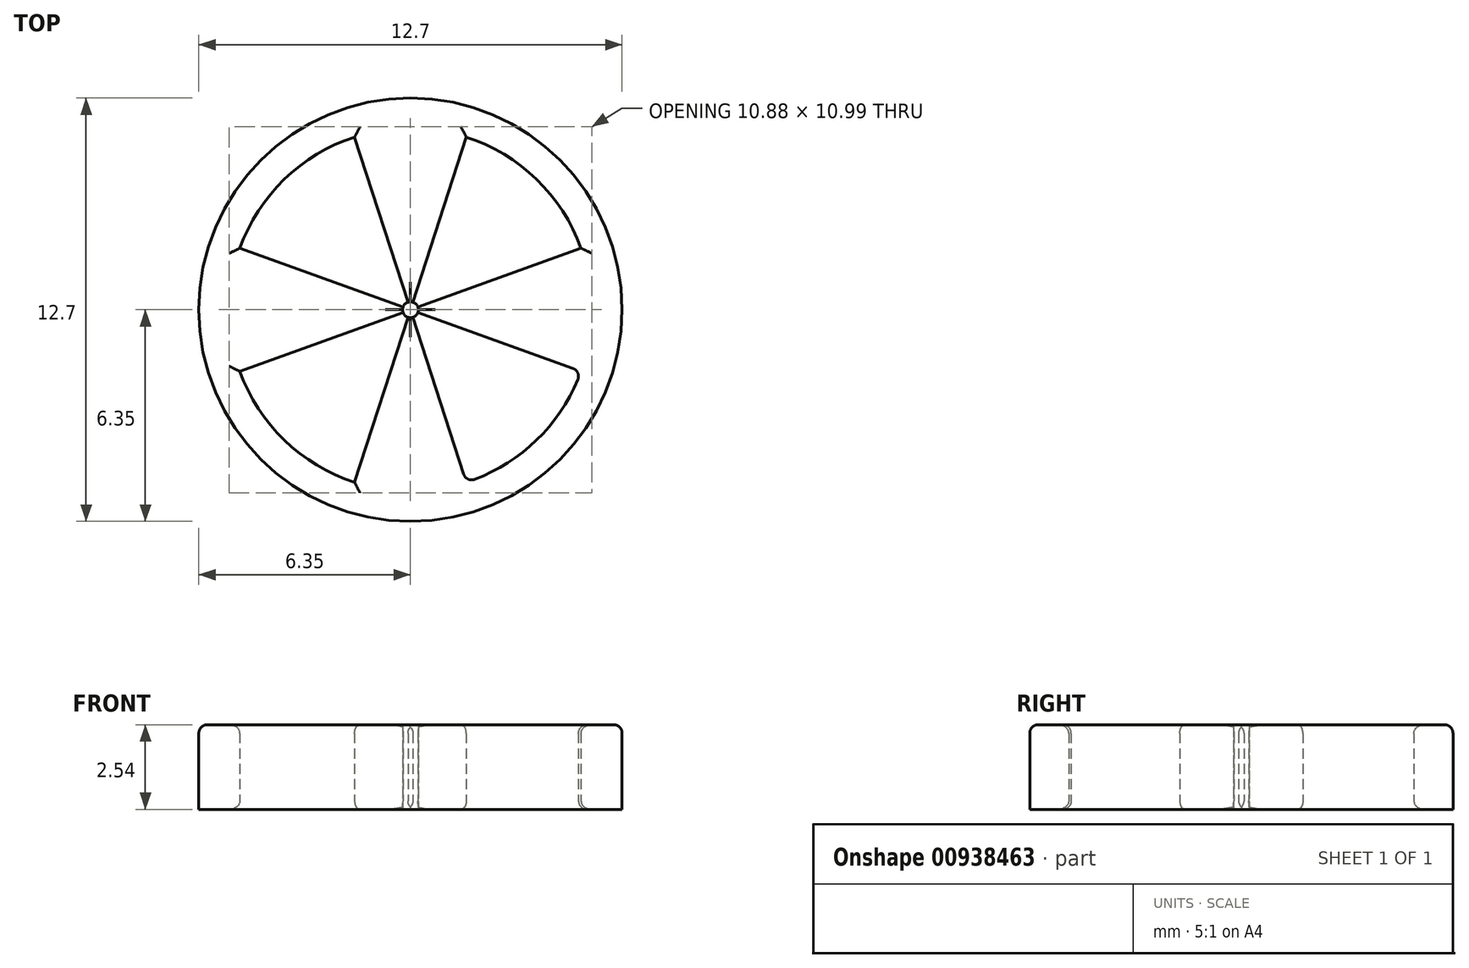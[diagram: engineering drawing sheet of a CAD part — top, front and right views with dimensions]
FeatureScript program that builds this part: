
annotation { "Feature Type Name" : "Feature", "Feature Type Description" : "" }
export const myFeature = defineFeature(function(context is Context, id is Id, definition is map)
    precondition{}
    {
        {
            var Q0;
            Q0=qCreatedBy(makeId("Top.planeOp"),FACE);
            var sketch = newSketch(context, id + "F0", { "sketchPlane" : qUnion([Q0])});
            skCircle(sketch, "E0", {"center": v(0, 0) * mm, "radius": 5.44 * mm});
            skLineSegment(sketch, "E1", {"start": v(0, 0) * mm, "end": v(-5.44, 0) * mm});
            skLineSegment(sketch, "E2", {"start": v(-5.44, 0) * mm, "end": v(5.44, 0) * mm});
            skLineSegment(sketch, "E3", {"start": v(0, 5.44) * mm, "end": v(0, -5.44) * mm});
            skLineSegment(sketch, "E4", {"start": v(0, 0) * mm, "end": v(-5.12, 1.85) * mm});
            skLineSegment(sketch, "E5.MirrorCS", {"start": v(0, 0) * mm, "end": v(5.12, 1.85) * mm});
            skLineSegment(sketch, "E6.MirrorCS", {"start": v(0, 0) * mm, "end": v(-5.12, -1.85) * mm});
            skLineSegment(sketch, "E7.MirrorCS", {"start": v(0, 0) * mm, "end": v(5.12, -1.85) * mm});
            skLineSegment(sketch, "E8", {"start": v(0, 0) * mm, "end": v(1.68, -5.18) * mm});
            skLineSegment(sketch, "E9.MirrorCS", {"start": v(0, 0) * mm, "end": v(-1.68, -5.18) * mm});
            skCircle(sketch, "E10.0", {"center": v(0, 0) * mm, "radius": 6.35 * mm});
            skCircle(sketch, "E11", {"center": v(0, 0) * mm, "radius": 0.24 * mm});
            skLineSegment(sketch, "E12.MirrorCS", {"start": v(0, 0) * mm, "end": v(1.68, 5.18) * mm});
            skLineSegment(sketch, "E13.MirrorCS", {"start": v(0, 0) * mm, "end": v(-1.68, 5.18) * mm});
            skSolve(sketch);
        }
        {
            var Q0;
            Q0=makeQuery(id+"F0.imprint","IMPRINT",FACE,{"disambiguationData":[TD([[makeQuery(id+"F0.imprint","IMPRINT",EDGE,{"derivedFrom":sQuery(id+"F0.wireOp",EDGE,"E10.0")}),1.0]])]});
            var Q1;
            {var subQ0=sQuery(id+"F0.wireOp",EDGE,"E3");var subQ1=sQuery(id+"F0.wireOp",EDGE,"E0");var subQ2=makeQuery(id+"F0.imprint","INTERSECT",VERTEX,{"disambiguationData":[OD(1.0)],"derivedFrom":[subQ1,subQ0]});Q1=makeQuery(id+"F0.imprint","IMPRINT",FACE,{"disambiguationData":[TD([[makeQuery(id+"F0.imprint","IMPRINT",EDGE,{"disambiguationData":[TD([[subQ2,-1.0]])],"derivedFrom":subQ1}),1.0]])]});}
            var Q2;
            {var subQ0=sQuery(id+"F0.wireOp",EDGE,"E9.MirrorCS");var subQ1=sQuery(id+"F0.wireOp",EDGE,"E0");var subQ2=makeQuery(id+"F0.imprint","INTERSECT",VERTEX,{"derivedFrom":[subQ1,subQ0]});Q2=makeQuery(id+"F0.imprint","IMPRINT",FACE,{"disambiguationData":[TD([[makeQuery(id+"F0.imprint","IMPRINT",EDGE,{"disambiguationData":[TD([[subQ2,-1.0]])],"derivedFrom":subQ1}),1.0]])]});}
            var Q3;
            {var subQ0=sQuery(id+"F0.wireOp",EDGE,"E4");var subQ1=sQuery(id+"F0.wireOp",EDGE,"E0");var subQ2=makeQuery(id+"F0.imprint","INTERSECT",VERTEX,{"derivedFrom":[subQ1,subQ0]});Q3=makeQuery(id+"F0.imprint","IMPRINT",FACE,{"disambiguationData":[TD([[makeQuery(id+"F0.imprint","IMPRINT",EDGE,{"disambiguationData":[TD([[subQ2,-1.0]])],"derivedFrom":subQ1}),1.0]])]});}
            var Q4;
            {var subQ0=sQuery(id+"F0.wireOp",EDGE,"E1");var subQ1=sQuery(id+"F0.wireOp",EDGE,"E0");var subQ2=makeQuery(id+"F0.imprint","INTERSECT",VERTEX,{"derivedFrom":[subQ1,subQ0]});Q4=makeQuery(id+"F0.imprint","IMPRINT",FACE,{"disambiguationData":[TD([[makeQuery(id+"F0.imprint","IMPRINT",EDGE,{"disambiguationData":[TD([[subQ2,-1.0]])],"derivedFrom":subQ1}),1.0]])]});}
            var Q5;
            {var subQ0=sQuery(id+"F0.wireOp",EDGE,"E5.MirrorCS");var subQ1=sQuery(id+"F0.wireOp",EDGE,"E0");var subQ2=makeQuery(id+"F0.imprint","INTERSECT",VERTEX,{"derivedFrom":[subQ1,subQ0]});Q5=makeQuery(id+"F0.imprint","IMPRINT",FACE,{"disambiguationData":[TD([[makeQuery(id+"F0.imprint","IMPRINT",EDGE,{"disambiguationData":[TD([[subQ2,1.0]])],"derivedFrom":subQ1}),1.0]])]});}
            var Q6;
            {var subQ0=sQuery(id+"F0.wireOp",EDGE,"E2");var subQ1=sQuery(id+"F0.wireOp",EDGE,"E0");var subQ2=makeQuery(id+"F0.imprint","INTERSECT",VERTEX,{"derivedFrom":[subQ1,subQ0]});Q6=makeQuery(id+"F0.imprint","IMPRINT",FACE,{"disambiguationData":[TD([[makeQuery(id+"F0.imprint","IMPRINT",EDGE,{"disambiguationData":[TD([[subQ2,1.0]])],"derivedFrom":subQ1}),1.0]])]});}
            var Q7;
            {var subQ0=sQuery(id+"F0.wireOp",EDGE,"E3");var subQ1=sQuery(id+"F0.wireOp",EDGE,"E0");var subQ2=makeQuery(id+"F0.imprint","INTERSECT",VERTEX,{"disambiguationData":[OD(0.0)],"derivedFrom":[subQ1,subQ0]});Q7=makeQuery(id+"F0.imprint","IMPRINT",FACE,{"disambiguationData":[TD([[makeQuery(id+"F0.imprint","IMPRINT",EDGE,{"disambiguationData":[TD([[subQ2,-1.0]])],"derivedFrom":subQ1}),1.0]])]});}
            var Q8;
            {var subQ0=sQuery(id+"F0.wireOp",EDGE,"E12.MirrorCS");var subQ1=sQuery(id+"F0.wireOp",EDGE,"E0");var subQ2=makeQuery(id+"F0.imprint","INTERSECT",VERTEX,{"derivedFrom":[subQ1,subQ0]});Q8=makeQuery(id+"F0.imprint","IMPRINT",FACE,{"disambiguationData":[TD([[makeQuery(id+"F0.imprint","IMPRINT",EDGE,{"disambiguationData":[TD([[subQ2,-1.0]])],"derivedFrom":subQ1}),1.0]])]});}
            extrude(context, id + "F1", {"entities" : qUnion([Q0, Q1, Q2, Q3, Q4, Q5, Q6, Q7, Q8]), "depth" : 2.54 * mm, "offsetDistance" : 25.4 * mm});
        }
        {
            var Q0;
            {var subQ0=sQuery(id+"F0.wireOp",EDGE,"E11");var subQ1=sQuery(id+"F0.wireOp",EDGE,"E1");var subQ2=makeQuery(id+"F0.imprint","INTERSECT",VERTEX,{"derivedFrom":[subQ1,subQ0]});Q0=makeQuery(id+"F0.imprint","IMPRINT",FACE,{"disambiguationData":[TD([[makeQuery(id+"F0.imprint","IMPRINT",EDGE,{"disambiguationData":[TD([[subQ2,-1.0]])],"derivedFrom":subQ0}),1.0]])]});}
            var Q1;
            {var subQ0=sQuery(id+"F0.wireOp",EDGE,"E11");var subQ1=sQuery(id+"F0.wireOp",EDGE,"E1");var subQ2=makeQuery(id+"F0.imprint","INTERSECT",VERTEX,{"derivedFrom":[subQ1,subQ0]});Q1=makeQuery(id+"F0.imprint","IMPRINT",FACE,{"disambiguationData":[TD([[makeQuery(id+"F0.imprint","IMPRINT",EDGE,{"disambiguationData":[TD([[subQ2,1.0]])],"derivedFrom":subQ0}),1.0]])]});}
            var Q2;
            {var subQ0=sQuery(id+"F0.wireOp",EDGE,"E11");var subQ1=sQuery(id+"F0.wireOp",EDGE,"E2");var subQ2=makeQuery(id+"F0.imprint","INTERSECT",VERTEX,{"derivedFrom":[subQ1,subQ0]});Q2=makeQuery(id+"F0.imprint","IMPRINT",FACE,{"disambiguationData":[TD([[makeQuery(id+"F0.imprint","IMPRINT",EDGE,{"disambiguationData":[TD([[subQ2,-1.0]])],"derivedFrom":subQ0}),1.0]])]});}
            var Q3;
            {var subQ0=sQuery(id+"F0.wireOp",EDGE,"E11");var subQ1=sQuery(id+"F0.wireOp",EDGE,"E2");var subQ2=makeQuery(id+"F0.imprint","INTERSECT",VERTEX,{"derivedFrom":[subQ1,subQ0]});Q3=makeQuery(id+"F0.imprint","IMPRINT",FACE,{"disambiguationData":[TD([[makeQuery(id+"F0.imprint","IMPRINT",EDGE,{"disambiguationData":[TD([[subQ2,1.0]])],"derivedFrom":subQ0}),1.0]])]});}
            var Q4;
            {var subQ0=sQuery(id+"F0.wireOp",EDGE,"E12.MirrorCS");var subQ3=sQuery(id+"F0.wireOp",EDGE,"E11");var subQ5=makeQuery(id+"F0.imprint","INTERSECT",VERTEX,{"derivedFrom":[subQ3,subQ0]});Q4=makeQuery(id+"F0.imprint","IMPRINT",FACE,{"disambiguationData":[TD([[makeQuery(id+"F0.imprint","IMPRINT",EDGE,{"disambiguationData":[TD([[subQ5,-1.0]])],"derivedFrom":subQ3}),1.0]])]});}
            var Q5;
            {var subQ0=sQuery(id+"F0.wireOp",EDGE,"E13.MirrorCS");var subQ3=sQuery(id+"F0.wireOp",EDGE,"E11");var subQ5=makeQuery(id+"F0.imprint","INTERSECT",VERTEX,{"derivedFrom":[subQ3,subQ0]});Q5=makeQuery(id+"F0.imprint","IMPRINT",FACE,{"disambiguationData":[TD([[makeQuery(id+"F0.imprint","IMPRINT",EDGE,{"disambiguationData":[TD([[subQ5,1.0]])],"derivedFrom":subQ3}),1.0]])]});}
            var Q6;
            {var subQ1=sQuery(id+"F0.wireOp",EDGE,"E6.MirrorCS");var subQ3=sQuery(id+"F0.wireOp",EDGE,"E11");var subQ4=makeQuery(id+"F0.imprint","INTERSECT",VERTEX,{"derivedFrom":[subQ1,subQ3]});Q6=makeQuery(id+"F0.imprint","IMPRINT",FACE,{"disambiguationData":[TD([[makeQuery(id+"F0.imprint","IMPRINT",EDGE,{"disambiguationData":[TD([[subQ4,-1.0]])],"derivedFrom":subQ3}),1.0]])]});}
            var Q7;
            {var subQ1=sQuery(id+"F0.wireOp",EDGE,"E7.MirrorCS");var subQ3=sQuery(id+"F0.wireOp",EDGE,"E11");var subQ4=makeQuery(id+"F0.imprint","INTERSECT",VERTEX,{"derivedFrom":[subQ1,subQ3]});Q7=makeQuery(id+"F0.imprint","IMPRINT",FACE,{"disambiguationData":[TD([[makeQuery(id+"F0.imprint","IMPRINT",EDGE,{"disambiguationData":[TD([[subQ4,1.0]])],"derivedFrom":subQ3}),1.0]])]});}
            var Q8;
            {var subQ0=sQuery(id+"F0.wireOp",EDGE,"E11");var subQ1=sQuery(id+"F0.wireOp",EDGE,"E3");var subQ2=makeQuery(id+"F0.imprint","INTERSECT",VERTEX,{"disambiguationData":[OD(0.0)],"derivedFrom":[subQ1,subQ0]});Q8=makeQuery(id+"F0.imprint","IMPRINT",FACE,{"disambiguationData":[TD([[makeQuery(id+"F0.imprint","IMPRINT",EDGE,{"disambiguationData":[TD([[subQ2,-1.0]])],"derivedFrom":subQ0}),1.0]])]});}
            var Q9;
            {var subQ0=sQuery(id+"F0.wireOp",EDGE,"E11");var subQ1=sQuery(id+"F0.wireOp",EDGE,"E3");var subQ2=makeQuery(id+"F0.imprint","INTERSECT",VERTEX,{"disambiguationData":[OD(0.0)],"derivedFrom":[subQ1,subQ0]});Q9=makeQuery(id+"F0.imprint","IMPRINT",FACE,{"disambiguationData":[TD([[makeQuery(id+"F0.imprint","IMPRINT",EDGE,{"disambiguationData":[TD([[subQ2,1.0]])],"derivedFrom":subQ0}),1.0]])]});}
            var Q10;
            {var subQ1=sQuery(id+"F0.wireOp",EDGE,"E4");var subQ3=sQuery(id+"F0.wireOp",EDGE,"E11");var subQ4=makeQuery(id+"F0.imprint","INTERSECT",VERTEX,{"derivedFrom":[subQ1,subQ3]});Q10=makeQuery(id+"F0.imprint","IMPRINT",FACE,{"disambiguationData":[TD([[makeQuery(id+"F0.imprint","IMPRINT",EDGE,{"disambiguationData":[TD([[subQ4,1.0]])],"derivedFrom":subQ3}),1.0]])]});}
            var Q11;
            {var subQ1=sQuery(id+"F0.wireOp",EDGE,"E5.MirrorCS");var subQ3=sQuery(id+"F0.wireOp",EDGE,"E11");var subQ4=makeQuery(id+"F0.imprint","INTERSECT",VERTEX,{"derivedFrom":[subQ1,subQ3]});Q11=makeQuery(id+"F0.imprint","IMPRINT",FACE,{"disambiguationData":[TD([[makeQuery(id+"F0.imprint","IMPRINT",EDGE,{"disambiguationData":[TD([[subQ4,-1.0]])],"derivedFrom":subQ3}),1.0]])]});}
            extrude(context, id + "F2", {"entities" : qUnion([Q0, Q1, Q2, Q3, Q4, Q5, Q6, Q7, Q8, Q9, Q10, Q11]), "depth" : 2.54 * mm, "offsetDistance" : 25.4 * mm});
        }
        {
            var Q0;
            Q0=makeQuery(id+"F1.opExtrude","CAP_EDGE",EDGE,{"disambiguationData":[OSD([sQuery(id+"F0.wireOp",EDGE,"E6.MirrorCS")])],"isStart":false});
            var Q1;
            Q1=makeQuery(id+"F1.opExtrude","CAP_EDGE",EDGE,{"disambiguationData":[OSD([sQuery(id+"F0.wireOp",EDGE,"E4")])],"isStart":false});
            var Q2;
            {var subQ0=sQuery(id+"F0.wireOp",EDGE,"E0");Q2=makeQuery(id+"F1.opExtrude","CAP_EDGE",EDGE,{"disambiguationData":[OSD([subQ0]),TDD([makeQuery(id+"F0.imprint","IMPRINT",EDGE,{"disambiguationData":[TD([[makeQuery(id+"F0.imprint","INTERSECT",VERTEX,{"derivedFrom":[subQ0,sQuery(id+"F0.wireOp",EDGE,"E6.MirrorCS")]}),-1.0]])],"derivedFrom":subQ0})])],"isStart":false});}
            var Q3;
            Q3=makeQuery(id+"F1.opExtrude","CAP_FACE",FACE,{"disambiguationData":[OSD([sQuery(id+"F0.wireOp",EDGE,"E0"),sQuery(id+"F0.wireOp",EDGE,"E4"),sQuery(id+"F0.wireOp",EDGE,"E5.MirrorCS"),sQuery(id+"F0.wireOp",EDGE,"E6.MirrorCS"),sQuery(id+"F0.wireOp",EDGE,"E7.MirrorCS"),sQuery(id+"F0.wireOp",EDGE,"E8"),sQuery(id+"F0.wireOp",EDGE,"E9.MirrorCS"),sQuery(id+"F0.wireOp",EDGE,"E10.0"),sQuery(id+"F0.wireOp",EDGE,"E11"),sQuery(id+"F0.wireOp",EDGE,"E12.MirrorCS"),sQuery(id+"F0.wireOp",EDGE,"E13.MirrorCS")])],"isStart":false});
            var Q4;
            Q4=makeQuery(id+"F1.opExtrude","CAP_EDGE",EDGE,{"disambiguationData":[OSD([sQuery(id+"F0.wireOp",EDGE,"E5.MirrorCS")])],"isStart":true});
            var Q5;
            Q5=makeQuery(id+"F1.opExtrude","CAP_EDGE",EDGE,{"disambiguationData":[OSD([sQuery(id+"F0.wireOp",EDGE,"E7.MirrorCS")])],"isStart":true});
            var Q6;
            {var subQ0=sQuery(id+"F0.wireOp",EDGE,"E0");Q6=makeQuery(id+"F1.opExtrude","SWEPT_FACE",FACE,{"disambiguationData":[OSD([subQ0]),TDD([makeQuery(id+"F0.imprint","IMPRINT",EDGE,{"disambiguationData":[TD([[makeQuery(id+"F0.imprint","INTERSECT",VERTEX,{"derivedFrom":[subQ0,sQuery(id+"F0.wireOp",EDGE,"E8")]}),-1.0]])],"derivedFrom":subQ0})])]});}
            var Q7;
            Q7=makeQuery(id+"F1.opExtrude","CAP_EDGE",EDGE,{"disambiguationData":[OSD([sQuery(id+"F0.wireOp",EDGE,"E8")])],"isStart":true});
            var Q8;
            Q8=makeQuery(id+"F1.opExtrude","CAP_EDGE",EDGE,{"disambiguationData":[OSD([sQuery(id+"F0.wireOp",EDGE,"E6.MirrorCS")])],"isStart":true});
            var Q9;
            Q9=makeQuery(id+"F1.opExtrude","CAP_EDGE",EDGE,{"disambiguationData":[OSD([sQuery(id+"F0.wireOp",EDGE,"E9.MirrorCS")])],"isStart":true});
            var Q10;
            {var subQ0=sQuery(id+"F0.wireOp",EDGE,"E0");Q10=makeQuery(id+"F1.opExtrude","CAP_EDGE",EDGE,{"disambiguationData":[OSD([subQ0]),TDD([makeQuery(id+"F0.imprint","IMPRINT",EDGE,{"disambiguationData":[TD([[makeQuery(id+"F0.imprint","INTERSECT",VERTEX,{"derivedFrom":[subQ0,sQuery(id+"F0.wireOp",EDGE,"E6.MirrorCS")]}),-1.0]])],"derivedFrom":subQ0})])],"isStart":true});}
            var Q11;
            Q11=makeQuery(id+"F1.opExtrude","CAP_EDGE",EDGE,{"disambiguationData":[OSD([sQuery(id+"F0.wireOp",EDGE,"E4")])],"isStart":true});
            var Q12;
            Q12=makeQuery(id+"F1.opExtrude","CAP_EDGE",EDGE,{"disambiguationData":[OSD([sQuery(id+"F0.wireOp",EDGE,"E13.MirrorCS")])],"isStart":true});
            var Q13;
            {var subQ0=sQuery(id+"F0.wireOp",EDGE,"E0");Q13=makeQuery(id+"F1.opExtrude","CAP_EDGE",EDGE,{"disambiguationData":[OSD([subQ0]),TDD([makeQuery(id+"F0.imprint","IMPRINT",EDGE,{"disambiguationData":[TD([[makeQuery(id+"F0.imprint","INTERSECT",VERTEX,{"derivedFrom":[subQ0,sQuery(id+"F0.wireOp",EDGE,"E13.MirrorCS")]}),-1.0]])],"derivedFrom":subQ0})])],"isStart":true});}
            var Q14;
            {var subQ0=sQuery(id+"F0.wireOp",EDGE,"E0");Q14=makeQuery(id+"F1.opExtrude","CAP_EDGE",EDGE,{"disambiguationData":[OSD([subQ0]),TDD([makeQuery(id+"F0.imprint","IMPRINT",EDGE,{"disambiguationData":[TD([[makeQuery(id+"F0.imprint","INTERSECT",VERTEX,{"derivedFrom":[subQ0,sQuery(id+"F0.wireOp",EDGE,"E5.MirrorCS")]}),-1.0]])],"derivedFrom":subQ0})])],"isStart":true});}
            var Q15;
            Q15=makeQuery(id+"F1.opExtrude","CAP_EDGE",EDGE,{"disambiguationData":[OSD([sQuery(id+"F0.wireOp",EDGE,"E12.MirrorCS")])],"isStart":true});
            fillet(context, id + "F3", {"entities" : qUnion([Q0, Q1, Q2, Q3, Q4, Q5, Q6, Q7, Q8, Q9, Q10, Q11, Q12, Q13, Q14, Q15]), "radius" : 0.25 * mm, "tangentPropagation" : true, "allowEdgeOverflow" : false});
        }
    });
